# Revit family: Korobka soedinitelnaya KVSK-Ex Sever (0Ex ia IIC T6 Ga)
name_source: partatom
category: Датчики
units: mm (PartAtom-declared; Revit-internal decimal feet)

## family parameters
Всегда вертикально = Да
Заголовок OmniClass = Communication and Data Processing Equipment
На основе рабочей плоскости = Нет
Номер OmniClass = 23.85.50.17
Общий = Нет
При загрузке вырезать с полостями = Нет
Размер круглого соединителя = Использовать диаметр
Сохранять ориентацию аннотаций = Нет
Тип детали = Нормальный
Точка принадлежности помещению = Нет

## types (1)
- Коробка соединительная КВСК Ех "СЕВЕР" 0EX IА IIC T6 GA
    ADSK_Единица измерения = шт.
    ADSK_Завод-изготовитель = ООО НПП «МАГНИТО-КОНТАКТ»
    ADSK_Масса = 1.2
    ADSK_Материал = Пластик черный
    ADSK_Наименование = КРУПНОГАБАРИТНАЯ ВЗРЫВОЗАЩИЩЁННАЯ СОЕДИНИТЕЛЬНАЯ КОРОБКА КВСК-Ex «СЕВЕР»
    ADSK_Наименование краткое = КВСК-Ex «СЕВЕР»
    ADSK_Обозначение = ПАШК.685552.002
    ADSK_Примечание = Маркировка взрывозащиты 0EX IА IIC T6 GA
    ADSK_Размер_Высота = 93 мм
    ADSK_Размер_Длина = 302 мм
    ADSK_Размер_Ширина = 197 мм
    URL = https://m-kontakt.ru
    Диапазон рабочих температур = от -65 до +70
    Изготовитель = ООО НПП «МАГНИТО-КОНТАКТ»
    Кабельные вводы = Да
    Описание = Коробки КВСК-Ех «СЕВЕР» предназначены для подключения к источнику питания и регистрирующей аппаратуре, имеющим искробезопасные электрические цепи по ГОСТ 31610.11-2014 (IEC 60079-11:2011) и искробезопасные параметры (уровень искробезопасной цепи и подгруппу электрооборудования), соответствующие условиям применения коробок во взрывоопасной зоне.Электрические зазоры, пути утечки и электрическая прочность изоляции коробки соответствуют требованиям ГОСТ 31610.0-2014 (IEC 60079-0:2011).

Коробки не содержат электрических элементов, способных накапливать энергию, опасную для поджигания газов категории IIB и IIC.

Фрикционная и электростатическая искробезопасность корпусов коробок обеспечивается выбором конструктивных материалов.

Коробки КВСК-Ех «СЕВЕР» относится к взрывозащищённому электрооборудованию группы II ГОСТ 31610.0-2014 (IEC 60079-0:2011) и предназначена для применения во взрывоопасных зонах в соответствии с установленной маркировкой взрывозащиты, требованиями ТР ТС 012/2011, ГОСТ IEC 60079-14:2013.

Возможные взрывоопасные зоны применения коробок КВСК-Ех «СЕВЕР», категории взрывоопасных смесей газов и паров с воздухом в соответствии с требованиями ГОСТ IEC 60079-10-1-2011, ГОСТ IEC 60079-20-1-2011, других нормативных документов, регламентирующих применение электрооборудования во взрывоопасных зонах.
    Отметка по умолчанию = 0 мм
    Переходное сопротивление двух контактов = не более 0,3
    Присоединительные размеры (длина) = 220 мм
    Присоединительные размеры (ширина) = 168 мм
    Срок службы = не менее 10 лет
    Степень защиты оболочки = IP66/IP67
